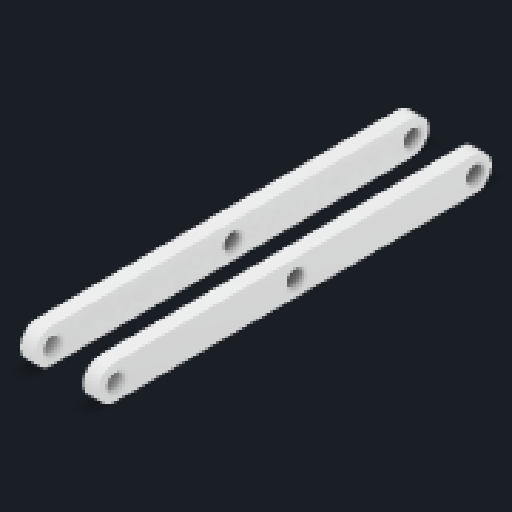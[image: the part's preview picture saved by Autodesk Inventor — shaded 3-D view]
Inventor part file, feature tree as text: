
AUTODESK INVENTOR PART (.ipt)
format: ipt  version: 2025.3 (Build 293356030, 356C)  size: 261,120 bytes
history: native  units: mm
features: sketch x2, extrude x2, hole x1
ambient origin geometry x8: Origin, YZ Plane, XZ Plane, XY Plane, X Axis, Y Axis, Z Axis, Center Point
bodies: Body1 (feature_tree)
feature tree (5):
  sketch  "Sketch1"  dims[d14=7.0mm d15=81.0mm]
  extrude  "Extrusión3"  Depth=7.0mm
  extrude  "Extrusión4"  Depth=16.0mm TaperAngle=0.0deg
  hole  "Agujero1"  [1 undecoded]
  sketch  "Boceto2"  dims[d16=3.0mm d17=16.0mm d18=0.0mm d19=10.0mm d20=0.0mm d21=3.4mm d22=6.0mm d23=6.3mm d24=2.0mm d25=90.0deg d26=8.0mm d27=20.594885mm]
note: 1 required parameter value undecoded (feature->parameter linkage not recoverable at this tier; creation-order binding heuristic only, values carry confidence <= 0.55)
